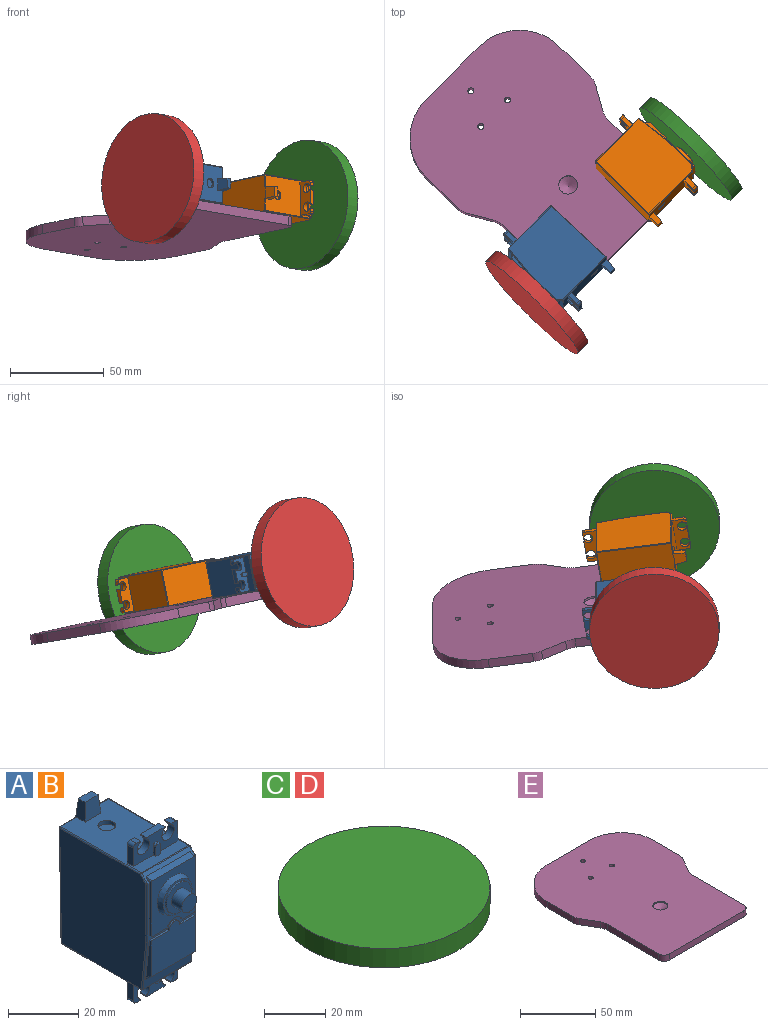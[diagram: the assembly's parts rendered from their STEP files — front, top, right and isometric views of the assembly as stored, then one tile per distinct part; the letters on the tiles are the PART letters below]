
ASSEMBLY  parts=5 mates=2
PART A: 118 faces, bbox 20.1x42.7x55.7 mm
  f0: plane 32.47x19.3mm, normal (0,0,1), area 537.9mm2, adj f39,f44,f54,f55,f56,f58,f59,f60
  f1: plane 10.03x10.03mm, normal (0,-1,0), area 51.1mm2, adj f2,f116
  f2: cylinder r=5.02mm len=10.03mm, axis (0,1,0), area 16mm2, adj f1,f3
  f3: plane 11.67x11.67mm, normal (0,-1,0), area 27.9mm2, adj f2,f4
  f4: cone r=7.18mm half-angle=20deg, axis (0,1,0), area 73.2mm2, adj f3,f16
  f5: plane 2.5x1.68mm, normal (0,0,-1), area 4.2mm2, adj f6,f18,f23,f67
  f6: plane 2.5x0.37mm, normal (-1,0,0), area 0.9mm2, adj f5,f7,f18,f23
  f7: cylinder r=2.5mm len=5mm, axis (0,1,0), area 33.1mm2, adj f6,f8,f18,f23
  f8: plane 2.5x0.37mm, normal (1,0,0), area 0.9mm2, adj f7,f9,f18,f23
  f9: plane 7.64x2.5mm, normal (0,0,-1), area 19.1mm2, adj f8,f10,f18,f23
  f10: plane 2.5x0.37mm, normal (-1,0,0), area 0.9mm2, adj f9,f11,f18,f23
  f11: cylinder r=2.5mm len=5mm, axis (0,1,0), area 33.1mm2, adj f10,f12,f18,f23
  f12: plane 2.5x0.37mm, normal (1,0,0), area 0.9mm2, adj f11,f13,f18,f23
  f13: plane 2.5x1.68mm, normal (0,0,-1), area 4.2mm2, adj f12,f18,f23,f66
  f14: plane 1x0.73mm, normal (0,0,-1), area 0.7mm2, adj f21,f23,f112,f115
  f15: plane 17.91x14.67mm, normal (0,-1,0), area 231.9mm2, adj f27,f28,f29,f30,f31,f32,f106,f107
  f16: plane 19.53x17.91mm, normal (0,-1,0), area 208.2mm2, adj f4,f24,f25,f26,f33,f34,f35,f104
  f17: plane 6.36x2.5mm, normal (-1,0,0), area 15.9mm2, adj f18,f23,f36,f66
  f18: plane 18x7.5mm, normal (0,1,0), area 94.4mm2, adj f5,f6,f7,f8,f9,f10,f11,f12
  f19: plane 6.36x2.5mm, normal (1,0,0), area 15.9mm2, adj f18,f23,f36,f67
  f20: plane 3.37x1mm, normal (1,0,0), area 3.4mm2, adj f21,f23,f36,f112
  f21: plane 4x2mm, normal (0,-1,0), area 7.8mm2, adj f14,f20,f22,f36,f112,f115
  f22: plane 3.37x1mm, normal (-1,0,0), area 3.4mm2, adj f21,f23,f36,f115
  f23: plane 18x7.5mm, normal (0,-1,0), area 86.6mm2, adj f5,f6,f7,f8,f9,f10,f11,f12
  f24: plane 6x0.64mm, normal (0,0,-1), area 3.8mm2, adj f16,f25,f37,f105
  f25: cylinder r=3.37mm len=6.23mm, axis (0,-1,0), area 5.1mm2, adj f16,f24,f26,f37
  f26: plane 4.92x0.64mm, normal (0,0,-1), area 3.1mm2, adj f16,f25,f37,f104
  f27: plane 5.94x0.64mm, normal (0,0,1), area 3.8mm2, adj f15,f28,f37,f107
  f28: cylinder r=2.1mm len=4.19mm, axis (0,-1,0), area 4.2mm2, adj f15,f27,f29,f37
  f29: plane 7.02x0.64mm, normal (0,0,1), area 4.5mm2, adj f15,f28,f37,f106
  f30: plane 17.15x2.21mm, normal (0,-0.71,-0.71), area 53.6mm2, adj f15,f38,f108,f109
  f31: plane 13.8x2.15mm, normal (1,0,0), area 16.9mm2, adj f15,f37,f38,f71,f107,f108
  f32: plane 13.8x2.15mm, normal (-1,0,0), area 16.9mm2, adj f15,f37,f38,f75,f106,f109
  f33: plane 19.17x1.54mm, normal (1,0,0), area 12.3mm2, adj f16,f37,f42,f74,f104,f110
  f34: plane 17.15x2.08mm, normal (0,-0.26,0.97), area 37mm2, adj f16,f42,f110,f111
  f35: plane 19.17x1.54mm, normal (-1,0,0), area 12.3mm2, adj f16,f37,f42,f84,f105,f111
  f36: plane 32.18x19.3mm, normal (0,0,-1), area 574.1mm2, adj f17,f18,f19,f20,f21,f22,f23,f87
  f37: plane 20.14x19.3mm, normal (0,-1,0), area 53.6mm2, adj f24,f25,f26,f27,f28,f29,f31,f32
  f38: plane 19.3x17.42mm, normal (0,-0.99,-0.11), area 79.7mm2, adj f30,f31,f32,f71,f75,f76,f86,f87
  f39: plane 18x7.5mm, normal (0,1,0), area 94.4mm2, adj f0,f44,f45,f46,f47,f48,f49,f50
  f40: plane 40.27x19.3mm, normal (0,1,-0.02), area 772.4mm2, adj f60,f61,f62,f80,f89,f97,f101,f103
  f41: plane 39.88x34.79mm, normal (1,0,0), area 1354.1mm2, adj f73,f76,f82,f83,f88,f89
  f42: plane 19.3x2.32mm, normal (0,-0.71,0.71), area 29.6mm2, adj f33,f34,f35,f74,f83,f84,f94,f95
  f43: plane 39.88x34.79mm, normal (-1,0,0), area 1354.1mm2, adj f85,f86,f95,f96,f100,f101
  f44: plane 6.36x2.5mm, normal (-1,0,0), area 15.9mm2, adj f0,f39,f55,f68
  f45: plane 2.5x1.68mm, normal (0,0,1), area 4.2mm2, adj f39,f46,f55,f68
  f46: plane 2.5x0.37mm, normal (1,0,0), area 0.9mm2, adj f39,f45,f47,f55
  f47: cylinder r=2.5mm len=5mm, axis (0,1,0), area 33.1mm2, adj f39,f46,f48,f55
  f48: plane 2.5x0.37mm, normal (-1,0,0), area 0.9mm2, adj f39,f47,f49,f55
  f49: plane 7.64x2.5mm, normal (0,0,1), area 19.1mm2, adj f39,f48,f50,f55
  f50: plane 2.5x0.37mm, normal (1,0,0), area 0.9mm2, adj f39,f49,f51,f55
  f51: cylinder r=2.5mm len=5mm, axis (0,1,0), area 33.1mm2, adj f39,f50,f52,f55
  f52: plane 2.5x0.37mm, normal (-1,0,0), area 0.9mm2, adj f39,f51,f53,f55
  f53: plane 2.5x1.68mm, normal (0,0,1), area 4.2mm2, adj f39,f52,f55,f65
  f54: plane 6.36x2.5mm, normal (1,0,0), area 15.9mm2, adj f0,f39,f55,f65
  f55: plane 18x7.5mm, normal (0,-1,0), area 86.6mm2, adj f0,f44,f45,f46,f47,f48,f49,f50
  f56: plane 4x2mm, normal (0,-1,0), area 7.8mm2, adj f0,f57,f58,f59,f113,f114
  f57: plane 1x0.73mm, normal (0,0,1), area 0.7mm2, adj f55,f56,f113,f114
  f58: plane 3.37x1mm, normal (1,0,0), area 3.4mm2, adj f0,f55,f56,f114
  f59: plane 3.37x1mm, normal (-1,0,0), area 3.4mm2, adj f0,f55,f56,f113
  f60: plane 6.75x3.82mm, normal (-1,0,0.09), area 20.8mm2, adj f0,f40,f61,f63,f64,f103
  f61: plane 6.35x6.35mm, normal (0,1,0.09), area 36.9mm2, adj f40,f60,f62,f64
  f62: plane 6.75x3.82mm, normal (1,0,0.09), area 20.8mm2, adj f0,f40,f61,f63,f64,f80
  f63: plane 6.35x6.35mm, normal (0,-1,0.09), area 36.9mm2, adj f0,f60,f62,f64
  f64: plane 5.24x2.7mm, normal (0,0,1), area 14.1mm2, adj f60,f61,f62,f63
  f65: cylinder r=1.14mm len=2.5mm, axis (0,1,0), area 4.5mm2, adj f39,f53,f54,f55
  f66: cylinder r=1.14mm len=2.5mm, axis (0,1,0), area 4.5mm2, adj f13,f17,f18,f23
  f67: cylinder r=1.14mm len=2.5mm, axis (0,1,0), area 4.5mm2, adj f5,f18,f19,f23
  f68: cylinder r=1.14mm len=2.5mm, axis (0,1,0), area 4.5mm2, adj f39,f44,f45,f55
  f69: cylinder r=2.54mm len=5.08mm, axis (0,0,1), area 20.3mm2, adj f0,f70
  f70: plane 5.08x5.08mm, normal (0,0,1), area 20.3mm2, adj f69
  f71: cylinder r=0.38mm len=0.7mm, axis (1,0,0), area 0mm2, adj f31,f37,f38,f72
  f72: sphere r=0.38mm, area 0mm2, adj f71,f73,f76
  f73: cylinder r=0.38mm len=20.14mm, axis (0,0,1), area 12.1mm2, adj f37,f41,f72,f77
  f74: cylinder r=0.38mm len=0.7mm, axis (1,0,0), area 0.2mm2, adj f33,f37,f42,f77
  f75: cylinder r=0.38mm len=0.7mm, axis (1,0,0), area 0mm2, adj f32,f37,f38,f78
  f76: cylinder r=0.38mm len=17.46mm, axis (0,-0.11,0.99), area 10.5mm2, adj f38,f41,f72,f79
  f77: sphere r=0.38mm, area 0.1mm2, adj f73,f74,f83
  f78: sphere r=0.38mm, area 0mm2, adj f75,f85,f86
  f79: sphere r=0.38mm, area 0.2mm2, adj f76,f87,f88
  f80: cylinder r=0.38mm len=6.48mm, axis (-1,0,0), area 3.9mm2, adj f0,f40,f62,f81
  f81: sphere r=0.38mm, area 0.2mm2, adj f80,f82,f89
  f82: cylinder r=0.38mm len=32.47mm, axis (0,-1,0), area 19.4mm2, adj f0,f41,f81,f90
  f83: cylinder r=0.38mm len=2.59mm, axis (0,0.71,0.71), area 2mm2, adj f41,f42,f77,f90
  f84: cylinder r=0.38mm len=0.7mm, axis (1,0,0), area 0.2mm2, adj f35,f37,f42,f91
  f85: cylinder r=0.38mm len=20.14mm, axis (0,0,1), area 12.1mm2, adj f37,f43,f78,f91
  f86: cylinder r=0.38mm len=17.46mm, axis (0,-0.11,0.99), area 10.5mm2, adj f38,f43,f78,f92
  f87: cylinder r=0.38mm len=19.3mm, axis (-1,0,0), area 10.7mm2, adj f36,f38,f79,f92
  f88: cylinder r=0.38mm len=32.18mm, axis (0,-1,0), area 19.3mm2, adj f36,f41,f79,f93
  f89: cylinder r=0.38mm len=39.88mm, axis (0,0.02,1), area 23.9mm2, adj f40,f41,f81,f93
  f90: sphere r=0.38mm, area 0.1mm2, adj f82,f83,f94
  f91: sphere r=0.38mm, area 0.1mm2, adj f84,f85,f95
  f92: sphere r=0.38mm, area 0.2mm2, adj f86,f87,f96
  f93: sphere r=0.38mm, area 0.2mm2, adj f88,f89,f97
  f94: cylinder r=0.38mm len=19.3mm, axis (-1,0,0), area 5.8mm2, adj f0,f42,f90,f98
  f95: cylinder r=0.38mm len=2.59mm, axis (0,0.71,0.71), area 2mm2, adj f42,f43,f91,f98
  f96: cylinder r=0.38mm len=32.18mm, axis (0,-1,0), area 19.3mm2, adj f36,f43,f92,f99
  f97: cylinder r=0.38mm len=19.3mm, axis (1,0,0), area 11.4mm2, adj f36,f40,f93,f99
  f98: sphere r=0.38mm, area 0.1mm2, adj f94,f95,f100
  f99: sphere r=0.38mm, area 0.2mm2, adj f96,f97,f101
  f100: cylinder r=0.38mm len=32.47mm, axis (0,-1,0), area 19.4mm2, adj f0,f43,f98,f102
  f101: cylinder r=0.38mm len=39.88mm, axis (0,-0.02,-1), area 23.9mm2, adj f40,f43,f99,f102
  f102: sphere r=0.38mm, area 0.2mm2, adj f100,f101,f103
  f103: cylinder r=0.38mm len=6.48mm, axis (-1,0,0), area 3.9mm2, adj f0,f40,f60,f102
  f104: cylinder r=0.38mm len=0.64mm, axis (0,-1,0), area 0.4mm2, adj f16,f26,f33,f37
  f105: cylinder r=0.38mm len=0.64mm, axis (0,-1,0), area 0.4mm2, adj f16,f24,f35,f37
  f106: cylinder r=0.38mm len=0.64mm, axis (0,-1,0), area 0.4mm2, adj f15,f29,f32,f37
  f107: cylinder r=0.38mm len=0.64mm, axis (0,-1,0), area 0.4mm2, adj f15,f27,f31,f37
  f108: cylinder r=0.38mm len=2.75mm, axis (0,-0.71,0.71), area 1.9mm2, adj f15,f30,f31,f38
  f109: cylinder r=0.38mm len=2.75mm, axis (0,-0.71,0.71), area 1.9mm2, adj f15,f30,f32,f38
  f110: cylinder r=0.38mm len=2.28mm, axis (0,-0.97,-0.26), area 1.2mm2, adj f16,f33,f34,f42
  f111: cylinder r=0.38mm len=2.28mm, axis (0,-0.97,-0.26), area 1.2mm2, adj f16,f34,f35,f42
  f112: cylinder r=0.64mm len=1mm, axis (0,1,0), area 1mm2, adj f14,f20,f21,f23
  f113: cylinder r=0.64mm len=1mm, axis (0,1,0), area 1mm2, adj f55,f56,f57,f59
  f114: cylinder r=0.64mm len=1mm, axis (0,1,0), area 1mm2, adj f55,f56,f57,f58
  f115: cylinder r=0.64mm len=1mm, axis (0,1,0), area 1mm2, adj f14,f21,f22,f23
  f116: cylinder r=2.98mm len=5.97mm, axis (0,1,0), area 78.6mm2, adj f1,f117
  f117: plane 5.97x5.97mm, normal (0,-1,0), area 28mm2, adj f116
PART B: same geometry as A
PART C: 3 faces, bbox 69x69x7.6 mm
  f0: cylinder r=34.5mm len=69mm, axis (0,0,-1), area 1651.8mm2, adj f1,f2
  f1: plane 69x69mm, normal (0,0,1), area 3739.3mm2, adj f0
  f2: plane 69x69mm, normal (0,0,-1), area 3739.3mm2, adj f0
PART D: same geometry as C
PART E: 23 faces, bbox 100x130x5 mm
  f0: plane 23.84x5mm, normal (1,0,0), area 119.2mm2, adj f2,f3,f11,f15
  f1: plane 23.84x5mm, normal (-1,0,0), area 119.2mm2, adj f2,f3,f12,f16
  f2: plane 130x100mm, normal (0,0,1), area 11205.2mm2, adj f0,f1,f4,f5,f6,f7,f8,f9
  f3: plane 130x100mm, normal (0,0,-1), area 11283.8mm2, adj f0,f1,f4,f5,f6,f7,f8,f9
  f4: plane 70x5mm, normal (0,-1,0), area 350mm2, adj f2,f3,f19,f20
  f5: plane 40x5mm, normal (0,1,0), area 200mm2, adj f2,f3,f11,f12
  f6: cylinder r=1.6mm len=5mm, axis (0,0,-1), area 50.3mm2, adj f2,f3
  f7: cylinder r=1.6mm len=5mm, axis (0,0,-1), area 50.3mm2, adj f2,f3
  f8: cylinder r=1.6mm len=5mm, axis (0,0,-1), area 50.3mm2, adj f2,f3
  f9: plane 48.35x5mm, normal (1,0,0), area 241.7mm2, adj f2,f3,f17,f19
  f10: plane 48.35x5mm, normal (-1,0,0), area 241.7mm2, adj f2,f3,f18,f20
  f11: cylinder r=30mm len=30mm, axis (0,0,-1), area 235.6mm2, adj f0,f2,f3,f5
  f12: cylinder r=30mm len=30mm, axis (0,0,1), area 235.6mm2, adj f1,f2,f3,f5
  f13: plane 12.9x7.37mm, normal (0.87,-0.5,0), area 74.3mm2, adj f2,f3,f15,f17
  f14: plane 12.9x7.37mm, normal (-0.87,-0.5,0), area 74.3mm2, adj f2,f3,f16,f18
  f15: cylinder r=10mm len=5mm, axis (0,0,-1), area 25.9mm2, adj f0,f2,f3,f13
  f16: cylinder r=10mm len=5mm, axis (0,0,-1), area 25.9mm2, adj f1,f2,f3,f14
  f17: cylinder r=10mm len=5mm, axis (0,0,-1), area 25.9mm2, adj f2,f3,f9,f13
  f18: cylinder r=10mm len=5mm, axis (0,0,-1), area 25.9mm2, adj f2,f3,f10,f14
  f19: cylinder r=5mm len=5mm, axis (0,0,1), area 39.3mm2, adj f2,f3,f4,f9
  f20: cylinder r=5mm len=5mm, axis (0,0,-1), area 39.3mm2, adj f2,f3,f4,f10
  f21: cone r=0mm half-angle=59deg, axis (0,0,1), area 91.6mm2, adj f22
  f22: cylinder r=5mm len=10mm, axis (0,0,1), area 31.4mm2, adj f2,f21
PLACE A rot(axis=(0.28,0.85,-0.45),93.8deg) t=(103.09,-70.43,74.12)mm
PLACE B rot(axis=(0.65,-0.22,0.72),141.8deg) t=(179.68,5.88,60.89)mm
PLACE C rot(axis=(-0.68,-0.34,-0.64),156.2deg) t=(188.9,-3.05,62.81)mm
PLACE D rot(axis=(-0.68,-0.34,-0.64),156.2deg) t=(106.96,-84.69,76.97)mm
PLACE E rot(axis=(-0.23,0.07,0.97),46.7deg) t=(111.16,-5.6,46.38)mm
MATE fastened D.f0 <-> A.f116  axis (0.7,0.7,-0.12) through (112.32,-79.36,76.04)mm
MATE fastened C.f0 <-> B.f116  axis (-0.7,-0.7,0.12) through (188.9,-3.05,62.81)mm
